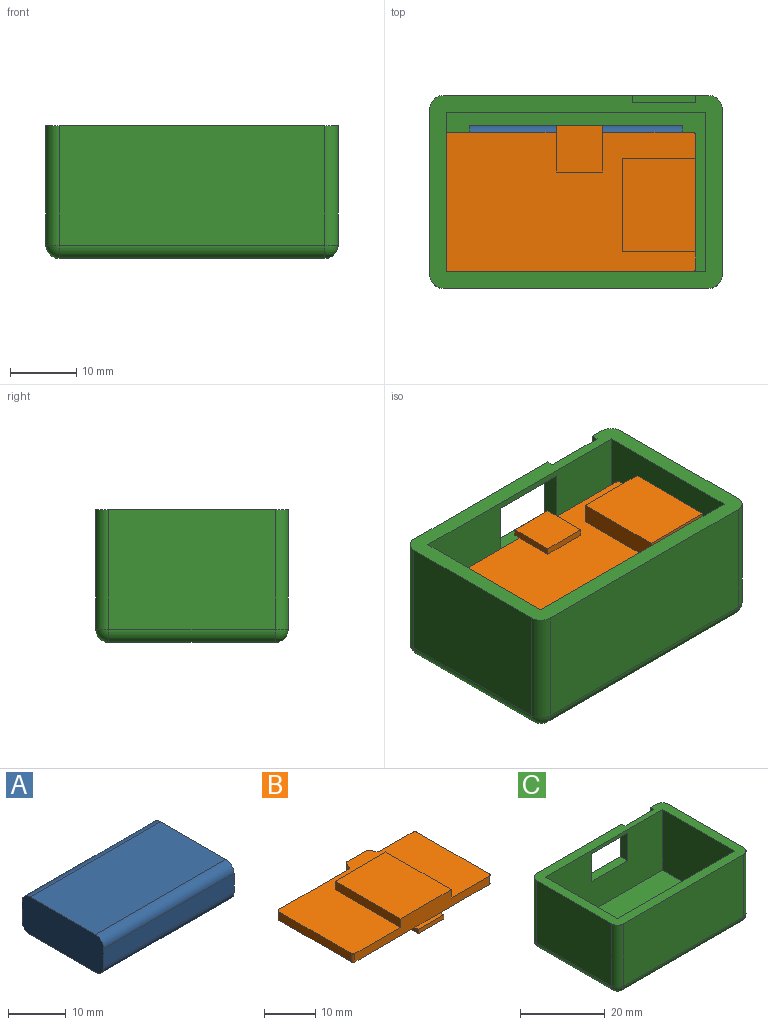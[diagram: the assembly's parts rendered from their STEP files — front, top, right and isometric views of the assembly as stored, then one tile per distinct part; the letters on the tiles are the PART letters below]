
ASSEMBLY  parts=3 mates=2
PART A: 10 faces, bbox 32x20x8 mm
  f0: plane 32x4mm, normal (0,1,0), area 128mm2, adj f1,f3,f7,f9
  f1: plane 20x8mm, normal (-1,0,0), area 156.6mm2, adj f0,f2,f4,f5,f6,f7,f8,f9
  f2: plane 32x4mm, normal (0,-1,0), area 128mm2, adj f1,f3,f6,f8
  f3: plane 20x8mm, normal (1,0,0), area 156.6mm2, adj f0,f2,f4,f5,f6,f7,f8,f9
  f4: plane 32x16mm, normal (0,0,1), area 512mm2, adj f1,f3,f8,f9
  f5: plane 32x16mm, normal (0,0,-1), area 512mm2, adj f1,f3,f6,f7
  f6: cylinder r=2mm len=32mm, axis (1,0,0), area 100.5mm2, adj f1,f2,f3,f5
  f7: cylinder r=2mm len=32mm, axis (-1,0,0), area 100.5mm2, adj f0,f1,f3,f5
  f8: cylinder r=2mm len=32mm, axis (-1,0,0), area 100.5mm2, adj f1,f2,f3,f4
  f9: cylinder r=2mm len=32mm, axis (1,0,0), area 100.5mm2, adj f0,f1,f3,f4
PART B: 32 faces, bbox 38x24x7 mm
  f0: plane 38x23mm, normal (0,0,1), area 559.8mm2, adj f1,f2,f3,f4,f5,f6,f7,f8
  f1: cylinder r=0.5mm len=2mm, axis (0,0,-1), area 1.1mm2, adj f0,f2,f16,f17
  f2: plane 19.19x2mm, normal (0,1,0), area 38.4mm2, adj f0,f1,f3,f17
  f3: cylinder r=0.5mm len=2mm, axis (0,0,-1), area 1.6mm2, adj f0,f2,f4,f17
  f4: plane 20x2mm, normal (-1,0,0), area 40mm2, adj f0,f3,f5,f17
  f5: cylinder r=0.5mm len=2mm, axis (0,0,-1), area 1.6mm2, adj f0,f4,f6,f17
  f6: plane 37x4mm, normal (0,-1,0), area 102mm2, adj f0,f5,f7,f17,f18,f20,f21,f27
  f7: cylinder r=0.5mm len=2mm, axis (0,0,-1), area 1.6mm2, adj f0,f6,f8,f17
  f8: plane 20x5mm, normal (1,0,0), area 82mm2, adj f0,f7,f9,f17,f28,f30,f31
  f9: cylinder r=0.5mm len=2mm, axis (0,0,-1), area 1.6mm2, adj f0,f8,f10,f17
  f10: plane 9.19x2mm, normal (0,1,0), area 18.4mm2, adj f0,f9,f11,f17
  f11: cylinder r=0.5mm len=2mm, axis (0,0,-1), area 1.1mm2, adj f0,f10,f12,f17
  f12: plane 2x1.45mm, normal (0.89,0.45,0), area 3.2mm2, adj f0,f11,f13,f17
  f13: cylinder r=0.5mm len=2mm, axis (0,0,-1), area 1.1mm2, adj f0,f12,f14,f17
  f14: plane 5.38x2mm, normal (0,1,0), area 10.8mm2, adj f0,f13,f15,f17
  f15: cylinder r=0.5mm len=2mm, axis (0,0,-1), area 1.1mm2, adj f0,f14,f16,f17
  f16: plane 2x1.45mm, normal (-0.89,0.45,0), area 3.2mm2, adj f0,f1,f15,f17
  f17: plane 38x23mm, normal (0,0,-1), area 615.8mm2, adj f1,f2,f3,f4,f5,f6,f7,f8
  f18: plane 18x2mm, normal (1,0,0), area 36mm2, adj f0,f6,f19,f21
  f19: plane 14x2mm, normal (0,1,0), area 28mm2, adj f0,f18,f20,f21
  f20: plane 18x2mm, normal (-1,0,0), area 36mm2, adj f0,f6,f19,f21
  f21: plane 18x14mm, normal (0,0,1), area 252mm2, adj f6,f18,f19,f20
  f22: plane 7x1mm, normal (1,0,0), area 7mm2, adj f17,f23,f25,f26,f27
  f23: plane 7x1mm, normal (0,-1,0), area 7mm2, adj f22,f24,f26,f27
  f24: plane 7x1mm, normal (-1,0,0), area 7mm2, adj f17,f23,f25,f26,f27
  f25: plane 7x1mm, normal (0,1,0), area 7mm2, adj f17,f22,f24,f26
  f26: plane 7x7mm, normal (0,0,-1), area 49mm2, adj f22,f23,f24,f25
  f27: plane 7x1mm, normal (0,0,1), area 7mm2, adj f6,f22,f23,f24
  f28: plane 11x3mm, normal (0,-1,0), area 33mm2, adj f8,f17,f29,f31
  f29: plane 14x3mm, normal (-1,0,0), area 42mm2, adj f17,f28,f30,f31
  f30: plane 11x3mm, normal (0,1,0), area 33mm2, adj f8,f17,f29,f31
  f31: plane 14x11mm, normal (0,0,-1), area 154mm2, adj f8,f28,f29,f30
PART C: 31 faces, bbox 44x29x20 mm
  f0: plane 40x18mm, normal (0,1,0), area 514.7mm2, adj f2,f16,f20,f22,f23,f24,f25,f26
  f1: plane 39x17.5mm, normal (0,-1,0), area 586.5mm2, adj f2,f7,f9,f10,f23,f24,f25,f26
  f2: plane 44x29mm, normal (0,0,1), area 327.1mm2, adj f0,f1,f3,f4,f5,f7,f8,f9
  f3: plane 25x18mm, normal (-1,0,0), area 450mm2, adj f2,f13,f19,f22
  f4: plane 40x18mm, normal (0,-1,0), area 720mm2, adj f2,f11,f13,f14
  f5: plane 25x18mm, normal (1,0,0), area 450mm2, adj f2,f11,f15,f16
  f6: plane 40x25mm, normal (0,0,-1), area 1000mm2, adj f14,f15,f19,f20
  f7: plane 24x17.5mm, normal (1,0,0), area 420mm2, adj f1,f2,f8,f10
  f8: plane 39x17.5mm, normal (0,1,0), area 682.5mm2, adj f2,f7,f9,f10
  f9: plane 24x17.5mm, normal (-1,0,0), area 420mm2, adj f1,f2,f8,f10
  f10: plane 39x24mm, normal (0,0,1), area 936mm2, adj f1,f7,f8,f9
  f11: cylinder r=2mm len=18mm, axis (0,0,1), area 56.5mm2, adj f2,f4,f5,f12
  f12: sphere r=2mm, area 6.3mm2, adj f11,f14,f15
  f13: cylinder r=2mm len=18mm, axis (0,0,-1), area 56.5mm2, adj f2,f3,f4,f17
  f14: cylinder r=2mm len=40mm, axis (1,0,0), area 125.7mm2, adj f4,f6,f12,f17
  f15: cylinder r=2mm len=25mm, axis (0,1,0), area 78.5mm2, adj f5,f6,f12,f18
  f16: cylinder r=2mm len=18mm, axis (0,0,-1), area 56.5mm2, adj f0,f2,f5,f18
  f17: sphere r=2mm, area 6.3mm2, adj f13,f14,f19
  f18: sphere r=2mm, area 6.3mm2, adj f15,f16,f20
  f19: cylinder r=2mm len=25mm, axis (0,-1,0), area 78.5mm2, adj f3,f6,f17,f21
  f20: cylinder r=2mm len=40mm, axis (-1,0,0), area 125.7mm2, adj f0,f6,f18,f21
  f21: sphere r=2mm, area 6.3mm2, adj f19,f20,f22
  f22: cylinder r=2mm len=18mm, axis (0,0,1), area 56.5mm2, adj f0,f2,f3,f21
  f23: plane 12x2.5mm, normal (0,0,-1), area 30mm2, adj f0,f1,f24,f26
  f24: plane 8x2.5mm, normal (-1,0,0), area 20mm2, adj f0,f1,f23,f25
  f25: plane 12x2.5mm, normal (0,0,1), area 30mm2, adj f0,f1,f24,f26
  f26: plane 8x2.5mm, normal (1,0,0), area 20mm2, adj f0,f1,f23,f25
  f27: plane 11.5x1mm, normal (-1,0,0), area 11.5mm2, adj f0,f2,f28,f30
  f28: plane 9.5x1mm, normal (0,0,1), area 9.5mm2, adj f0,f27,f29,f30
  f29: plane 11.5x1mm, normal (1,0,0), area 11.5mm2, adj f0,f2,f28,f30
  f30: plane 11.5x9.5mm, normal (0,1,0), area 109.2mm2, adj f2,f27,f28,f29
PLACE A t=(48.15,-18.14,2.5)mm
PLACE B rot(axis=(1,0,0),180deg) t=(-30.94,13.54,14.5)mm
PLACE C t=(37.26,47.05,0)mm
MATE fastened B.f21 <-> A.f4  axis (0,0,-1) through (0,0,10.5)mm
MATE fastened A.f5 <-> C.f10  axis (0,0,-1) through (0,0,2.5)mm
